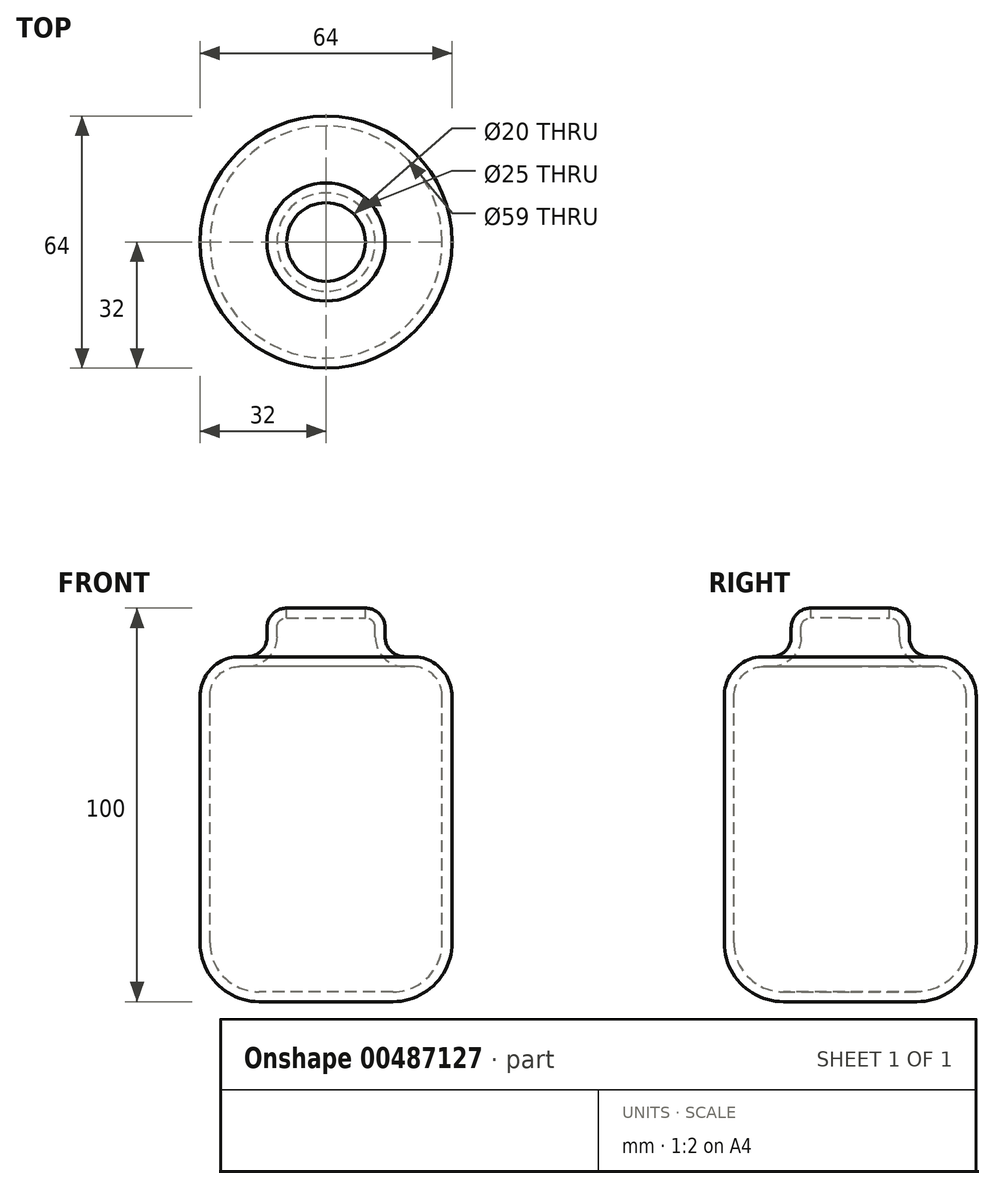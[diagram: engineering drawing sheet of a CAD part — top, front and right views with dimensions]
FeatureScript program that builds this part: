
annotation { "Feature Type Name" : "Feature", "Feature Type Description" : "" }
export const myFeature = defineFeature(function(context is Context, id is Id, definition is map)
    precondition{}
    {
        {
            var Q0;
            Q0=qCreatedBy(makeId("Front.planeOp"),FACE);
            var sketch = newSketch(context, id + "F0", { "sketchPlane" : qUnion([Q0])});
            skLineSegment(sketch, "E0", {"start": v(0, 50) * mm, "end": v(0, -50) * mm});
            skLineSegment(sketch, "E1", {"start": v(0, 50) * mm, "end": v(-10, 50) * mm});
            skLineSegment(sketch, "E2", {"start": v(-15, 45) * mm, "end": v(-15, 42.64) * mm});
            skLineSegment(sketch, "E3", {"start": v(-20, 37.64) * mm, "end": v(-22, 37.64) * mm});
            skLineSegment(sketch, "E4", {"start": v(-32, 27.64) * mm, "end": v(-32, -35) * mm});
            skLineSegment(sketch, "E5", {"start": v(-17, -50) * mm, "end": v(0, -50) * mm});
            skPoint(sketch, "E6.visualSharp", {"position": v(-15, 50) * mm});
            skArc(sketch, "E6.filletArc", {"start": v(-10, 50) * mm, "mid": v(-13.54, 48.54) * mm, "end": v(-15, 45) * mm});
            skPoint(sketch, "E7.visualSharp", {"position": v(-32, 37.64) * mm});
            skArc(sketch, "E7.filletArc", {"start": v(-22, 37.64) * mm, "mid": v(-29.07, 34.7) * mm, "end": v(-32, 27.64) * mm});
            skPoint(sketch, "E8.visualSharp", {"position": v(-32, -50) * mm});
            skArc(sketch, "E8.filletArc", {"start": v(-32, -35) * mm, "mid": v(-27.6, -45.6) * mm, "end": v(-17, -50) * mm});
            skPoint(sketch, "E9.visualSharp", {"position": v(-15, 37.64) * mm});
            skArc(sketch, "E9.filletArc", {"start": v(-20, 37.64) * mm, "mid": v(-16.46, 39.1) * mm, "end": v(-15, 42.64) * mm});
            skSolve(sketch);
        }
        {
            var Q0;
            Q0=makeQuery(id+"F0.imprint","IMPRINT",FACE,{"disambiguationData":[TD([[makeQuery(id+"F0.imprint","IMPRINT",EDGE,{"derivedFrom":sQuery(id+"F0.wireOp",EDGE,"E0")}),-1.0]])]});
            var Q1;
            Q1=sQuery(id+"F0.wireOp",EDGE,"E0");
            revolve(context, id + "F1", {"entities" : qUnion([Q0]), "axis" : qUnion([Q1]), "revolveType" : RevolveType.FULL});
        }
        {
            var Q0;
            Q0=makeQuery(id+"F1.opRevolve","SWEPT_FACE",FACE,{"disambiguationData":[OSD([sQuery(id+"F0.wireOp",EDGE,"E1")])]});
            shell(context, id + "F2", {"entities" : qUnion([Q0]), "thickness" : 2.5 * mm});
        }
    });
